AUTODESK INVENTOR PART (.ipt)
format: ipt  version: 2024.1 (Build 281209000, 209)  size: 312,320 bytes
history: native  units: mm
features: other x10, reference x7, sketch x5, projected_geometry x4, extrude x3, plane x2, hole x2, mirror x1
ambient origin geometry x8: Origin, YZ Plane, XZ Plane, XY Plane, X Axis, Y Axis, Z Axis, Center Point
bodies: Volumenkörper1 (feature_tree)
feature tree (34):
  plane  "Arbeitsebene1"
  extrude  "Extrusion1"  Depth=3.0mm
  hole  "Bohrung1"  [1 undecoded]
  plane  "Arbeitsebene2"
  mirror  "Spiegeln1"
  extrude  "Extrusion4"  Depth=3.5mm
  hole  "Bohrung4"  [1 undecoded]
  extrude  "Extrusion5"  Depth=20.0mm
  sketch  "Skizze1"  dims[d0=3.0mm d1=3.0mm]
  reference  "Referenz1"
  reference  "Referenz2"
  reference  "Referenz3"
  sketch  "Skizze3"  dims[d4=15.0mm d5=15.0mm]
  projected_geometry  "Projizierte Kontur2"
  sketch  "Skizze6"  dims[d6=10.0mm d7=0.0mm]
  projected_geometry  "Projizierte Kontur4"
  sketch  "Skizze8"  dims[d10=2.8mm d11=6.0mm d12=6.5mm d13=3.5mm d14=90.0deg d15=8.0mm d16=20.594885mm d42=1.5mm]
  reference  "Referenz7"
  projected_geometry  "Projizierte Kontur6"
  reference  "Referenz8"
  sketch  "Skizze9"  dims[d43=1.5mm d44=50.0mm d45=20.0mm d46=20.0mm d47=0.0mm d48=0.0mm d56=5.0mm d57=2.8mm d58=6.0mm d59=6.5mm d60=3.5mm d61=90.0deg d62=20.0mm d63=0.0mm d64=20.0mm d65=0.0mm d66=0.0mm]
  reference  "Referenz9"
  projected_geometry  "Projizierte Kontur7"
  reference  "Referenz10"
  other  "Assembly_Planktoscope_Uc2version_wormdrive_V3.iam"
  other  "60_Planktoscope_RaspiScreenHolder_v0:1"
  other  "60_Planktoscope_Base_half_wormdrive_1:1"
  other  "60_Planktoscope_Base_half_wormdrive_1_MIR:1"
  other  "Assembly_MicroscopeInABox_v0.iam"
  other  "MIAB_Case_v0:1"
  other  "60_Planktoscope_Illuminationsource:1"
  other  "Assembly_XYZ_Stage_Micrometer_ontop_lightsheet:1"
  other  "40_XYZstage_micrometer_motorized_nema8_samplemount_lightsheet_screwed:2"
  other  "60_Planktoscope_Electronicsholder:1"
note: 2 required parameter values undecoded (feature->parameter linkage not recoverable at this tier; creation-order binding heuristic only, values carry confidence <= 0.55)
